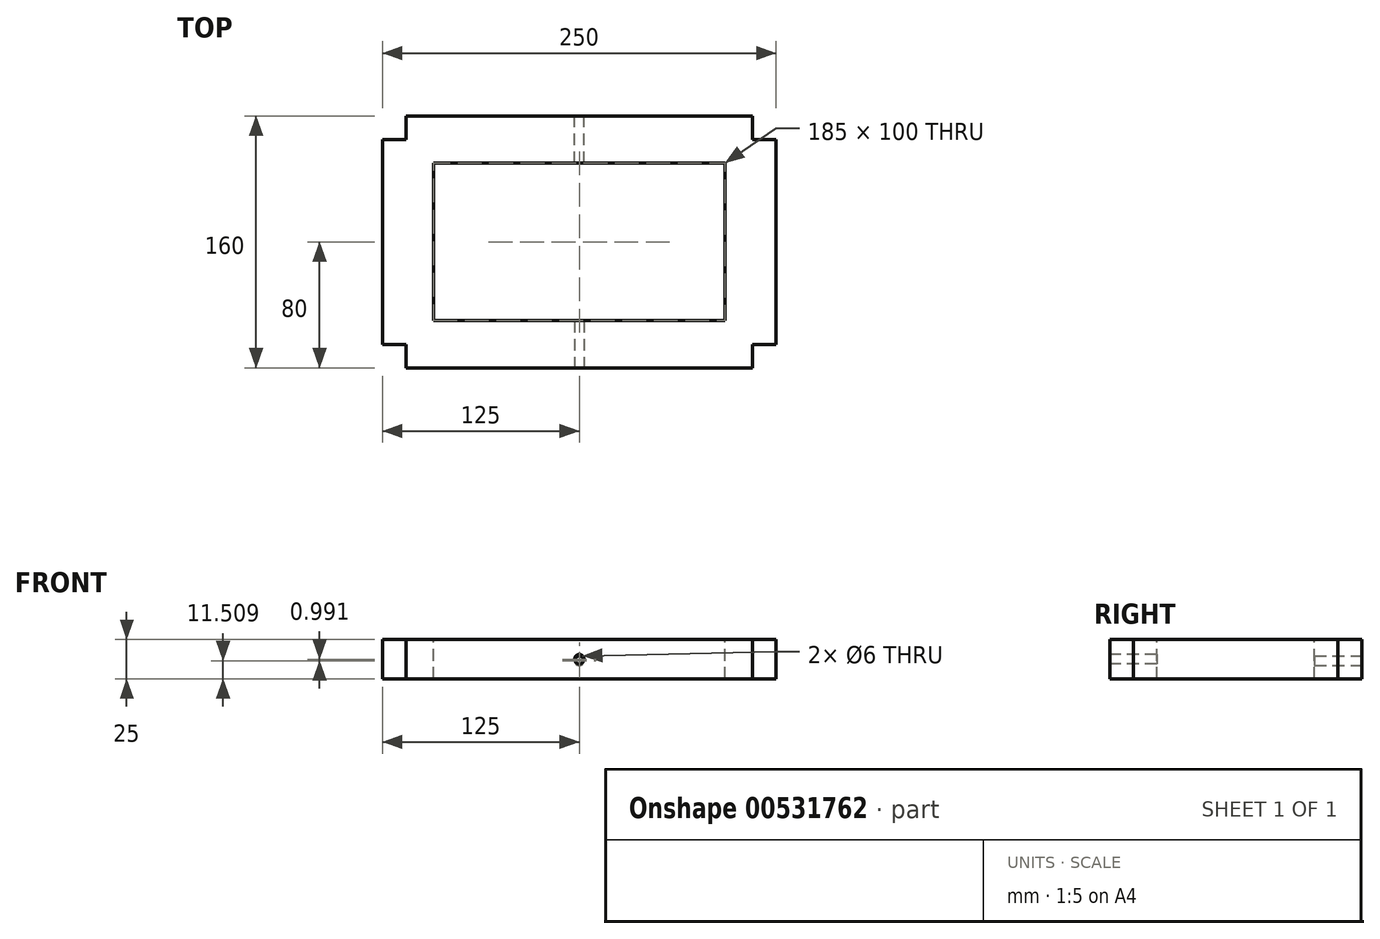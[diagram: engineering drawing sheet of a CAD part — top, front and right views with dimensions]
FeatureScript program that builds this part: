
annotation { "Feature Type Name" : "Feature", "Feature Type Description" : "" }
export const myFeature = defineFeature(function(context is Context, id is Id, definition is map)
    precondition{}
    {
        {
            var Q0;
            Q0=qCreatedBy(makeId("Top.planeOp"),FACE);
            var sketch = newSketch(context, id + "F0", { "sketchPlane" : qUnion([Q0])});
            skLineSegment(sketch, "E0.bottom", {"start": v(125, -80) * mm, "end": v(-125, -80) * mm});
            skLineSegment(sketch, "E0.top", {"start": v(125, 80) * mm, "end": v(-125, 80) * mm});
            skLineSegment(sketch, "E0.left", {"start": v(125, -80) * mm, "end": v(125, 80) * mm});
            skLineSegment(sketch, "E0.right", {"start": v(-125, -80) * mm, "end": v(-125, 80) * mm});
            skPoint(sketch, "E0.middle", {"position": v(0, 0) * mm});
            skSolve(sketch);
        }
        {
            var Q0;
            Q0=makeQuery(id+"F0.imprint","IMPRINT",FACE,{"disambiguationData":[TD([[makeQuery(id+"F0.imprint","IMPRINT",EDGE,{"derivedFrom":sQuery(id+"F0.wireOp",EDGE,"E0.bottom")}),-1.0]])]});
            extrude(context, id + "F1", {"entities" : qUnion([Q0]), "depth" : 25 * mm, "offsetDistance" : 25 * mm});
        }
        {
            var Q0;
            Q0=makeQuery(id+"F1.opExtrude","CAP_FACE",FACE,{"disambiguationData":[OSD([sQuery(id+"F0.wireOp",EDGE,"E0.bottom"),sQuery(id+"F0.wireOp",EDGE,"E0.top"),sQuery(id+"F0.wireOp",EDGE,"E0.left"),sQuery(id+"F0.wireOp",EDGE,"E0.right")])],"isStart":false});
            var sketch = newSketch(context, id + "F2", { "sketchPlane" : qUnion([Q0])});
            skLineSegment(sketch, "E1.bottom", {"start": v(-125, 80) * mm, "end": v(-110, 80) * mm});
            skLineSegment(sketch, "E1.top", {"start": v(-125, 65) * mm, "end": v(-110, 65) * mm});
            skLineSegment(sketch, "E1.left", {"start": v(-125, 80) * mm, "end": v(-125, 65) * mm});
            skLineSegment(sketch, "E1.right", {"start": v(-110, 80) * mm, "end": v(-110, 65) * mm});
            skLineSegment(sketch, "E2.bottom", {"start": v(125, 80) * mm, "end": v(110, 80) * mm});
            skLineSegment(sketch, "E2.top", {"start": v(125, 65) * mm, "end": v(110, 65) * mm});
            skLineSegment(sketch, "E2.left", {"start": v(125, 80) * mm, "end": v(125, 65) * mm});
            skLineSegment(sketch, "E2.right", {"start": v(110, 80) * mm, "end": v(110, 65) * mm});
            skLineSegment(sketch, "E3.bottom", {"start": v(125, -80) * mm, "end": v(110, -80) * mm});
            skLineSegment(sketch, "E3.top", {"start": v(125, -65) * mm, "end": v(110, -65) * mm});
            skLineSegment(sketch, "E3.left", {"start": v(125, -80) * mm, "end": v(125, -65) * mm});
            skLineSegment(sketch, "E3.right", {"start": v(110, -80) * mm, "end": v(110, -65) * mm});
            skLineSegment(sketch, "E4.bottom", {"start": v(-125, -80) * mm, "end": v(-110, -80) * mm});
            skLineSegment(sketch, "E4.top", {"start": v(-125, -65) * mm, "end": v(-110, -65) * mm});
            skLineSegment(sketch, "E4.left", {"start": v(-125, -80) * mm, "end": v(-125, -65) * mm});
            skLineSegment(sketch, "E4.right", {"start": v(-110, -80) * mm, "end": v(-110, -65) * mm});
            skSolve(sketch);
        }
        {
            var Q0;
            Q0 = qSketchRegion(id + "F2", true);
            extrude(context, id + "F3", {"entities" : qUnion([Q0]), "operationType" : NewBodyOperationType.REMOVE, "oppositeDirection" : true, "depth" : 25 * mm, "offsetDistance" : 25 * mm});
        }
        {
            var Q0;
            Q0=makeQuery(id+"F1.opExtrude","CAP_FACE",FACE,{"disambiguationData":[OSD([sQuery(id+"F0.wireOp",EDGE,"E0.bottom"),sQuery(id+"F0.wireOp",EDGE,"E0.top"),sQuery(id+"F0.wireOp",EDGE,"E0.left"),sQuery(id+"F0.wireOp",EDGE,"E0.right")])],"isStart":false});
            var sketch = newSketch(context, id + "F4", { "sketchPlane" : qUnion([Q0])});
            skLineSegment(sketch, "E5.bottom", {"start": v(92.5, 50) * mm, "end": v(-92.5, 50) * mm});
            skLineSegment(sketch, "E5.top", {"start": v(92.5, -50) * mm, "end": v(-92.5, -50) * mm});
            skLineSegment(sketch, "E5.left", {"start": v(92.5, 50) * mm, "end": v(92.5, -50) * mm});
            skLineSegment(sketch, "E5.right", {"start": v(-92.5, 50) * mm, "end": v(-92.5, -50) * mm});
            skPoint(sketch, "E5.middle", {"position": v(0, 0) * mm});
            skSolve(sketch);
        }
        {
            var Q0;
            Q0 = qSketchRegion(id + "F4", true);
            extrude(context, id + "F5", {"entities" : qUnion([Q0]), "operationType" : NewBodyOperationType.REMOVE, "oppositeDirection" : true, "depth" : 25 * mm, "offsetDistance" : 25 * mm});
        }
        {
            var Q0;
            Q0=makeQuery(id+"F1.opExtrude","SWEPT_FACE",FACE,{"disambiguationData":[OSD([sQuery(id+"F0.wireOp",EDGE,"E0.bottom")])]});
            var sketch = newSketch(context, id + "F6", { "sketchPlane" : qUnion([Q0])});
            skCircle(sketch, "E6", {"center": v(0, 12.5) * mm, "radius": 3 * mm});
            skSolve(sketch);
        }
        {
            var Q0;
            Q0 = qSketchRegion(id + "F6", true);
            extrude(context, id + "F7", {"entities" : qUnion([Q0]), "operationType" : NewBodyOperationType.REMOVE, "oppositeDirection" : true, "depth" : 40 * mm, "offsetDistance" : 25 * mm});
        }
        {
            var Q0;
            Q0=makeQuery(id+"F1.opExtrude","SWEPT_FACE",FACE,{"disambiguationData":[OSD([sQuery(id+"F0.wireOp",EDGE,"E0.top")])]});
            var sketch = newSketch(context, id + "F8", { "sketchPlane" : qUnion([Q0])});
            skCircle(sketch, "E7", {"center": v(0, 11.5) * mm, "radius": 3 * mm});
            skSolve(sketch);
        }
        {
            var Q0;
            Q0 = qSketchRegion(id + "F8", true);
            extrude(context, id + "F9", {"entities" : qUnion([Q0]), "operationType" : NewBodyOperationType.REMOVE, "oppositeDirection" : true, "depth" : 40 * mm, "offsetDistance" : 25 * mm});
        }
    });
